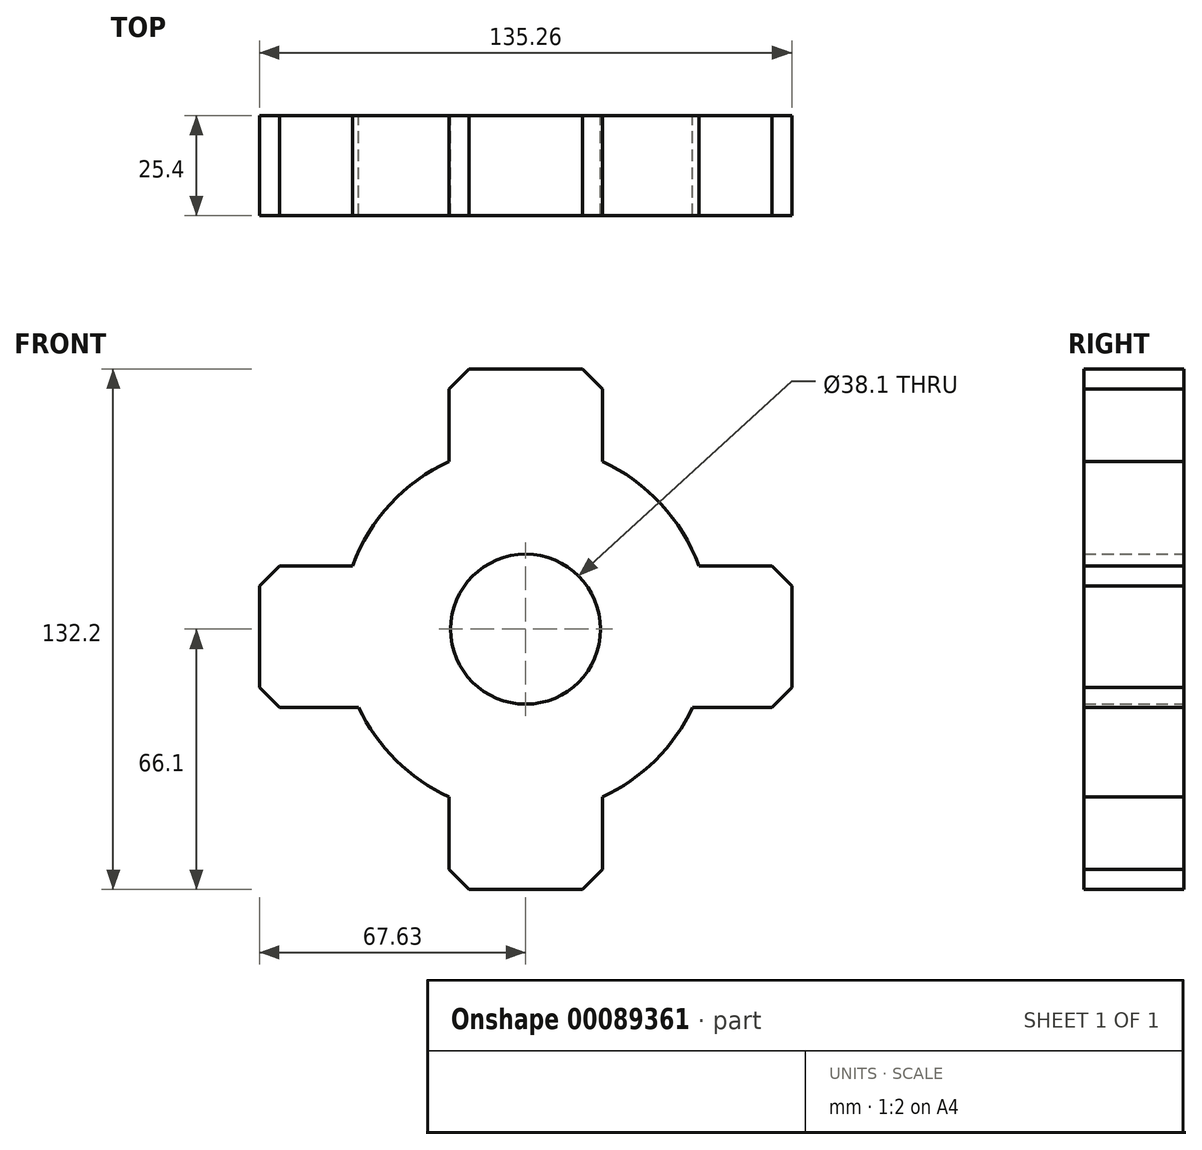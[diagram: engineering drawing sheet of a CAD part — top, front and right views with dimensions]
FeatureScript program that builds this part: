
annotation { "Feature Type Name" : "Feature", "Feature Type Description" : "" }
export const myFeature = defineFeature(function(context is Context, id is Id, definition is map)
    precondition{}
    {
        {
            var Q0;
            Q0=qCreatedBy(makeId("Front.planeOp"),FACE);
            var sketch = newSketch(context, id + "F0", { "sketchPlane" : qUnion([Q0])});
            skArc(sketch, "E0", {"start": v(-42.41, -19.9) * mm, "mid": v(-32.95, -33.3) * mm, "end": v(-19.44, -42.62) * mm});
            skLineSegment(sketch, "E1", {"start": v(-43.99, 16.12) * mm, "end": v(-67.63, 16.12) * mm});
            skLineSegment(sketch, "E2", {"start": v(-67.63, 16.12) * mm, "end": v(-67.63, -19.9) * mm});
            skLineSegment(sketch, "E3", {"start": v(-67.63, -19.9) * mm, "end": v(-42.41, -19.9) * mm});
            skLineSegment(sketch, "E4.MirrorCS", {"start": v(67.63, -19.9) * mm, "end": v(42.41, -19.9) * mm});
            skLineSegment(sketch, "E5.MirrorCS", {"start": v(43.99, 16.12) * mm, "end": v(67.63, 16.12) * mm});
            skLineSegment(sketch, "E6.MirrorCS", {"start": v(67.63, 16.12) * mm, "end": v(67.63, -19.9) * mm});
            skArc(sketch, "E7.trimOffspring", {"start": v(43.99, 16.12) * mm, "mid": v(34.38, 31.82) * mm, "end": v(19.48, 42.6) * mm});
            skLineSegment(sketch, "E8", {"start": v(-19.44, 42.62) * mm, "end": v(-19.44, 66.1) * mm});
            skLineSegment(sketch, "E9", {"start": v(-19.44, 66.1) * mm, "end": v(19.48, 66.1) * mm});
            skLineSegment(sketch, "E10", {"start": v(19.48, 66.1) * mm, "end": v(19.48, 42.6) * mm});
            skLineSegment(sketch, "E11.MirrorCS", {"start": v(-19.44, -42.62) * mm, "end": v(-19.44, -66.1) * mm});
            skLineSegment(sketch, "E12.MirrorCS", {"start": v(-19.44, -66.1) * mm, "end": v(19.48, -66.1) * mm});
            skLineSegment(sketch, "E13.MirrorCS", {"start": v(19.48, -66.1) * mm, "end": v(19.48, -42.6) * mm});
            skArc(sketch, "E14.trimOffspring", {"start": v(-19.44, 42.62) * mm, "mid": v(-34.37, 31.83) * mm, "end": v(-43.99, 16.12) * mm});
            skArc(sketch, "E15.trimOffspring", {"start": v(19.48, -42.6) * mm, "mid": v(32.96, -33.29) * mm, "end": v(42.41, -19.9) * mm});
            skSolve(sketch);
        }
        {
            var Q0;
            Q0=makeQuery(id+"F0.imprint","IMPRINT",FACE,{"disambiguationData":[TD([[makeQuery(id+"F0.imprint","IMPRINT",EDGE,{"derivedFrom":sQuery(id+"F0.wireOp",EDGE,"E0")}),1.0]])]});
            extrude(context, id + "F1", {"entities" : qUnion([Q0]), "depth" : 25.4 * mm});
        }
        {
            var Q0;
            Q0=qCreatedBy(makeId("Front.planeOp"),FACE);
            var sketch = newSketch(context, id + "F2", { "sketchPlane" : qUnion([Q0])});
            skCircle(sketch, "E16", {"center": v(0, 0) * mm, "radius": 16.87 * mm});
            skSolve(sketch);
        }
        {
            var Q0;
            Q0=sQuery(id+"F2.wireOp",VERTEX,"E16.center");
            var Q1;
            Q1=makeQuery(id+"F1.opExtrude","SWEPT_BODY",BODY,{"disambiguationData":[OSD([sQuery(id+"F0.wireOp",EDGE,"E0"),sQuery(id+"F0.wireOp",EDGE,"E1"),sQuery(id+"F0.wireOp",EDGE,"E2"),sQuery(id+"F0.wireOp",EDGE,"E3"),sQuery(id+"F0.wireOp",EDGE,"E4.MirrorCS"),sQuery(id+"F0.wireOp",EDGE,"E5.MirrorCS"),sQuery(id+"F0.wireOp",EDGE,"E6.MirrorCS"),sQuery(id+"F0.wireOp",EDGE,"E7.trimOffspring"),sQuery(id+"F0.wireOp",EDGE,"E8"),sQuery(id+"F0.wireOp",EDGE,"E9"),sQuery(id+"F0.wireOp",EDGE,"E10"),sQuery(id+"F0.wireOp",EDGE,"E11.MirrorCS"),sQuery(id+"F0.wireOp",EDGE,"E12.MirrorCS"),sQuery(id+"F0.wireOp",EDGE,"E13.MirrorCS"),sQuery(id+"F0.wireOp",EDGE,"E14.trimOffspring"),sQuery(id+"F0.wireOp",EDGE,"E15.trimOffspring")])]});
            hole(context, id + "F3", {"style" : HoleStyle.SIMPLE, "endStyle" : HoleEndStyle.THROUGH, "oppositeDirection" : true, "holeDiameter" : 38.1 * mm, "locations" : qUnion([Q0]), "scope" : qUnion([Q1]), "isTappedThrough" : true});
        }
        {
            var Q0;
            Q0=makeQuery(id+"F1.opExtrude","SWEPT_EDGE",EDGE,{"disambiguationData":[OSD([sQuery(id+"F0.wireOp",EDGE,"E9"),sQuery(id+"F0.wireOp",EDGE,"E10")])]});
            chamfer(context, id + "F4", {"entities" : qUnion([Q0]), "width" : 5.08 * mm, "tangentPropagation" : true});
        }
        {
            var Q0;
            Q0=makeQuery(id+"F1.opExtrude","SWEPT_EDGE",EDGE,{"disambiguationData":[OSD([sQuery(id+"F0.wireOp",EDGE,"E8"),sQuery(id+"F0.wireOp",EDGE,"E9")])]});
            chamfer(context, id + "F5", {"entities" : qUnion([Q0]), "width" : 5.08 * mm, "tangentPropagation" : true});
        }
        {
            var Q0;
            Q0=makeQuery(id+"F1.opExtrude","SWEPT_EDGE",EDGE,{"disambiguationData":[OSD([sQuery(id+"F0.wireOp",EDGE,"E1"),sQuery(id+"F0.wireOp",EDGE,"E2")])]});
            chamfer(context, id + "F6", {"entities" : qUnion([Q0]), "width" : 5.08 * mm, "tangentPropagation" : true});
        }
        {
            var Q0;
            Q0=makeQuery(id+"F1.opExtrude","SWEPT_EDGE",EDGE,{"disambiguationData":[OSD([sQuery(id+"F0.wireOp",EDGE,"E2"),sQuery(id+"F0.wireOp",EDGE,"E3")])]});
            chamfer(context, id + "F7", {"entities" : qUnion([Q0]), "width" : 5.08 * mm, "tangentPropagation" : true});
        }
        {
            var Q0;
            Q0=makeQuery(id+"F1.opExtrude","SWEPT_EDGE",EDGE,{"disambiguationData":[OSD([sQuery(id+"F0.wireOp",EDGE,"E12.MirrorCS"),sQuery(id+"F0.wireOp",EDGE,"E13.MirrorCS")])]});
            chamfer(context, id + "F8", {"entities" : qUnion([Q0]), "width" : 5.08 * mm, "tangentPropagation" : true});
        }
        {
            var Q0;
            Q0=makeQuery(id+"F1.opExtrude","SWEPT_EDGE",EDGE,{"disambiguationData":[OSD([sQuery(id+"F0.wireOp",EDGE,"E11.MirrorCS"),sQuery(id+"F0.wireOp",EDGE,"E12.MirrorCS")])]});
            chamfer(context, id + "F9", {"entities" : qUnion([Q0]), "width" : 5.08 * mm, "tangentPropagation" : true});
        }
        {
            var Q0;
            Q0=makeQuery(id+"F1.opExtrude","SWEPT_EDGE",EDGE,{"disambiguationData":[OSD([sQuery(id+"F0.wireOp",EDGE,"E5.MirrorCS"),sQuery(id+"F0.wireOp",EDGE,"E6.MirrorCS")])]});
            chamfer(context, id + "F10", {"entities" : qUnion([Q0]), "width" : 5.08 * mm, "tangentPropagation" : true});
        }
        {
            var Q0;
            Q0=makeQuery(id+"F1.opExtrude","SWEPT_EDGE",EDGE,{"disambiguationData":[OSD([sQuery(id+"F0.wireOp",EDGE,"E4.MirrorCS"),sQuery(id+"F0.wireOp",EDGE,"E6.MirrorCS")])]});
            chamfer(context, id + "F11", {"entities" : qUnion([Q0]), "width" : 5.08 * mm, "tangentPropagation" : true});
        }
    });
